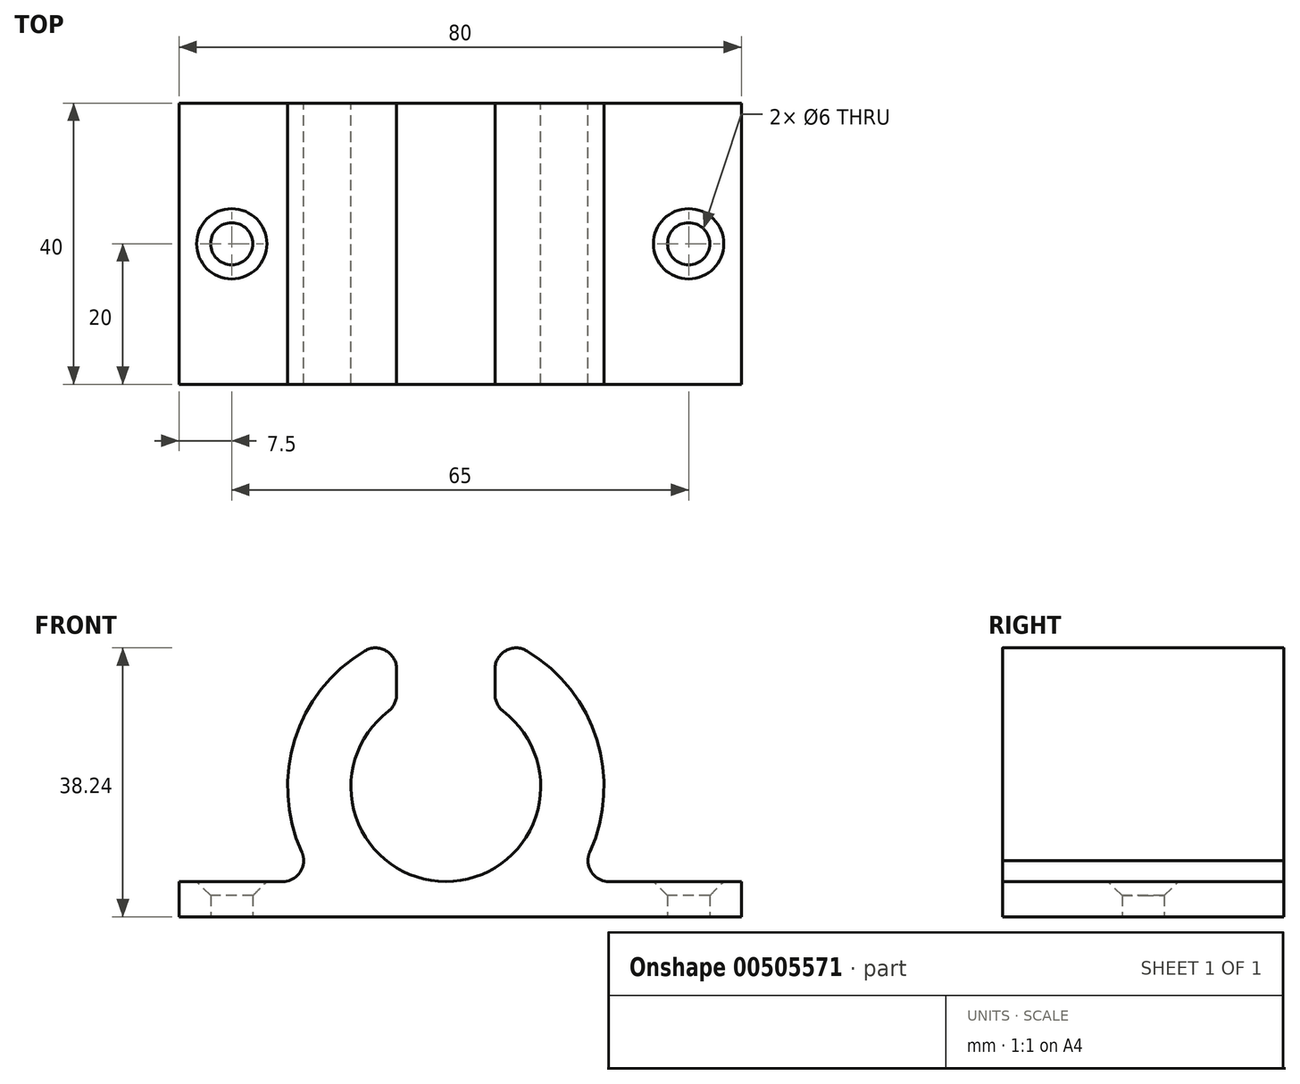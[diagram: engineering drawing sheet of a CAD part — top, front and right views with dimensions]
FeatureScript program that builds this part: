
annotation { "Feature Type Name" : "Feature", "Feature Type Description" : "" }
export const myFeature = defineFeature(function(context is Context, id is Id, definition is map)
    precondition{}
    {
        {
            var Q0;
            Q0=qCreatedBy(makeId("Top.planeOp"),FACE);
            var sketch = newSketch(context, id + "F0", { "sketchPlane" : qUnion([Q0])});
            skLineSegment(sketch, "E0.bottom", {"start": v(0, 0) * mm, "end": v(80, 0) * mm});
            skLineSegment(sketch, "E0.top", {"start": v(0, -40) * mm, "end": v(80, -40) * mm});
            skLineSegment(sketch, "E0.left", {"start": v(0, 0) * mm, "end": v(0, -40) * mm});
            skLineSegment(sketch, "E0.right", {"start": v(80, 0) * mm, "end": v(80, -40) * mm});
            skLineSegment(sketch, "E1.bottom", {"start": v(65, -35) * mm, "end": v(15, -35) * mm});
            skLineSegment(sketch, "E1.top", {"start": v(65, -5) * mm, "end": v(15, -5) * mm});
            skLineSegment(sketch, "E1.left", {"start": v(65, -35) * mm, "end": v(65, -5) * mm});
            skLineSegment(sketch, "E1.right", {"start": v(15, -35) * mm, "end": v(15, -5) * mm});
            skPoint(sketch, "E1.middle", {"position": v(40, -20) * mm});
            skPoint(sketch, "E1.middle.positionSnap0", {"position": v(80, -20) * mm});
            skPoint(sketch, "E1.middle.positionSnap1", {"position": v(40, 0) * mm});
            skPoint(sketch, "E1.centerSnap0", {"position": v(80, -20) * mm});
            skPoint(sketch, "E1.centerSnap1", {"position": v(40, 0) * mm});
            skCircle(sketch, "E2", {"center": v(7.5, -20) * mm, "radius": 3 * mm});
            skPoint(sketch, "E2.centerSnap0", {"position": v(0, -20) * mm});
            skLineSegment(sketch, "E3", {"start": v(40, 0) * mm, "end": v(40, -40) * mm, "construction": true});
            skCircle(sketch, "E4.MirrorC", {"center": v(72.5, -20) * mm, "radius": 3 * mm});
            skLineSegment(sketch, "E5", {"start": v(7.5, -20) * mm, "end": v(0, -20) * mm, "construction": true});
            skLineSegment(sketch, "E6", {"start": v(7.5, -20) * mm, "end": v(15, -20) * mm, "construction": true});
            skSolve(sketch);
        }
        {
            var Q0;
            Q0=makeQuery(id+"F0.imprint","IMPRINT",FACE,{"disambiguationData":[TD([[makeQuery(id+"F0.imprint","IMPRINT",EDGE,{"derivedFrom":sQuery(id+"F0.wireOp",EDGE,"E0.bottom")}),-1.0]])]});
            var Q1;
            Q1=makeQuery(id+"F0.imprint","IMPRINT",FACE,{"disambiguationData":[TD([[makeQuery(id+"F0.imprint","IMPRINT",EDGE,{"derivedFrom":sQuery(id+"F0.wireOp",EDGE,"E1.bottom")}),-1.0]])]});
            extrude(context, id + "F1", {"entities" : qUnion([Q0, Q1]), "depth" : 5 * mm});
        }
        {
            var Q0;
            Q0=makeQuery(id+"F1.opExtrude","CAP_EDGE",EDGE,{"disambiguationData":[OSD([sQuery(id+"F0.wireOp",EDGE,"E2")])],"isStart":false});
            var Q1;
            Q1=makeQuery(id+"F1.opExtrude","CAP_EDGE",EDGE,{"disambiguationData":[OSD([sQuery(id+"F0.wireOp",EDGE,"E4.MirrorC")])],"isStart":false});
            chamfer(context, id + "F2", {"entities" : qUnion([Q0, Q1]), "width" : 2 * mm, "tangentPropagation" : true});
        }
        {
            var Q0;
            Q0=makeQuery(id+"F1.opExtrude","CAP_EDGE",EDGE,{"disambiguationData":[OSD([sQuery(id+"F0.wireOp",EDGE,"E0.bottom")])],"isStart":false});
            cPoint(context, id + "F3", {"entities" : qUnion([Q0]), "parameter" : 0.5});
        }
        {
            var Q0;
            Q0 = qCreatedBy(id + "F3" ,VERTEX);
            var Q1;
            Q1=makeQuery(id+"F1.opExtrude","SWEPT_FACE",FACE,{"disambiguationData":[OSD([sQuery(id+"F0.wireOp",EDGE,"E0.bottom")])]});
            cPlane(context, id + "F4", {"entities" : qUnion([Q0, Q1]), "cplaneType" : CPlaneType.PLANE_POINT, "offset" : 25 * mm, "width" : 150 * mm, "height" : 150 * mm});
        }
        {
            var Q0;
            Q0=qCreatedBy(id+"F4.planeOp",FACE);
            var sketch = newSketch(context, id + "F5", { "sketchPlane" : qUnion([Q0])});
            skArc(sketch, "E7", {"start": v(-44.95, 30.04) * mm, "mid": v(-37.95, 5) * mm, "end": v(-30.95, 30.04) * mm});
            skArc(sketch, "E8.0", {"start": v(-44.95, 39.88) * mm, "mid": v(-58.68, 27.26) * mm, "end": v(-58.17, 8.63) * mm});
            skLineSegment(sketch, "E9", {"start": v(-37.95, 18.5) * mm, "end": v(-37.95, 49.9) * mm, "construction": true});
            skLineSegment(sketch, "E10.0", {"start": v(-30.95, 30.04) * mm, "end": v(-30.95, 39.88) * mm});
            skLineSegment(sketch, "E11.0", {"start": v(-44.95, 30.04) * mm, "end": v(-44.95, 39.88) * mm});
            skLineSegment(sketch, "E12", {"start": v(-58.17, 8.63) * mm, "end": v(-58.17, 0) * mm});
            skLineSegment(sketch, "E13.MirrorCS", {"start": v(-17.74, 8.63) * mm, "end": v(-17.74, 0) * mm});
            skArc(sketch, "E14.trimOffspring", {"start": v(-17.74, 8.63) * mm, "mid": v(-17.23, 27.26) * mm, "end": v(-30.95, 39.88) * mm});
            skLineSegment(sketch, "E15", {"start": v(-58.17, 0) * mm, "end": v(-17.74, 0) * mm});
            skSolve(sketch);
        }
        {
            var Q0;
            Q0=makeQuery(id+"F5.imprint","IMPRINT",FACE,{"disambiguationData":[TD([[makeQuery(id+"F5.imprint","IMPRINT",EDGE,{"derivedFrom":sQuery(id+"F5.wireOp",EDGE,"E7")}),-1.0]])]});
            extrude(context, id + "F6", {"entities" : qUnion([Q0]), "operationType" : NewBodyOperationType.ADD, "oppositeDirection" : true, "depth" : 40 * mm});
        }
        {
            var Q0;
            Q0=makeQuery(id+"F6.opExtrude","SWEPT_EDGE",EDGE,{"disambiguationData":[OSD([sQuery(id+"F5.wireOp",EDGE,"E8.0"),sQuery(id+"F5.wireOp",EDGE,"E11.0")])]});
            var Q1;
            Q1=makeQuery(id+"F6.opExtrude","SWEPT_EDGE",EDGE,{"disambiguationData":[OSD([sQuery(id+"F5.wireOp",EDGE,"E10.0"),sQuery(id+"F5.wireOp",EDGE,"E14.trimOffspring")])]});
            var Q2;
            Q2=makeQuery(id+"F6.opExtrude","SWEPT_EDGE",EDGE,{"disambiguationData":[OSD([sQuery(id+"F5.wireOp",EDGE,"E7"),sQuery(id+"F5.wireOp",EDGE,"E11.0")])]});
            var Q3;
            Q3=makeQuery(id+"F6.opExtrude","SWEPT_EDGE",EDGE,{"disambiguationData":[OSD([sQuery(id+"F5.wireOp",EDGE,"E7"),sQuery(id+"F5.wireOp",EDGE,"E10.0")])]});
            var Q4;
            Q4=makeQuery(id+"F6.opExtrude","SWEPT_EDGE",EDGE,{"disambiguationData":[OSD([sQuery(id+"F5.wireOp",EDGE,"E8.0"),sQuery(id+"F5.wireOp",EDGE,"E12")])]});
            var Q5;
            Q5=makeQuery(id+"F6.boolean.opBoolean","INTERSECT",EDGE,{"derivedFrom":[makeQuery(id+"F1.opExtrude","CAP_FACE",FACE,{"disambiguationData":[OSD([sQuery(id+"F0.wireOp",EDGE,"E0.bottom"),sQuery(id+"F0.wireOp",EDGE,"E0.top"),sQuery(id+"F0.wireOp",EDGE,"E0.left"),sQuery(id+"F0.wireOp",EDGE,"E0.right"),sQuery(id+"F0.wireOp",EDGE,"E2"),sQuery(id+"F0.wireOp",EDGE,"E4.MirrorC")])],"isStart":false}),makeQuery(id+"F6.opExtrude","SWEPT_FACE",FACE,{"disambiguationData":[OSD([sQuery(id+"F5.wireOp",EDGE,"E12")])]})]});
            var Q6;
            Q6=makeQuery(id+"F6.opExtrude","SWEPT_EDGE",EDGE,{"disambiguationData":[OSD([sQuery(id+"F5.wireOp",EDGE,"E13.MirrorCS"),sQuery(id+"F5.wireOp",EDGE,"E14.trimOffspring")])]});
            var Q7;
            Q7=makeQuery(id+"F6.boolean.opBoolean","INTERSECT",EDGE,{"derivedFrom":[makeQuery(id+"F1.opExtrude","CAP_FACE",FACE,{"disambiguationData":[OSD([sQuery(id+"F0.wireOp",EDGE,"E0.bottom"),sQuery(id+"F0.wireOp",EDGE,"E0.top"),sQuery(id+"F0.wireOp",EDGE,"E0.left"),sQuery(id+"F0.wireOp",EDGE,"E0.right"),sQuery(id+"F0.wireOp",EDGE,"E2"),sQuery(id+"F0.wireOp",EDGE,"E4.MirrorC")])],"isStart":false}),makeQuery(id+"F6.opExtrude","SWEPT_FACE",FACE,{"disambiguationData":[OSD([sQuery(id+"F5.wireOp",EDGE,"E13.MirrorCS")])]})]});
            fillet(context, id + "F7", {"entities" : qUnion([Q0, Q1, Q2, Q3, Q4, Q5, Q6, Q7]), "radius" : 3 * mm, "tangentPropagation" : true, "allowEdgeOverflow" : false});
        }
    });
